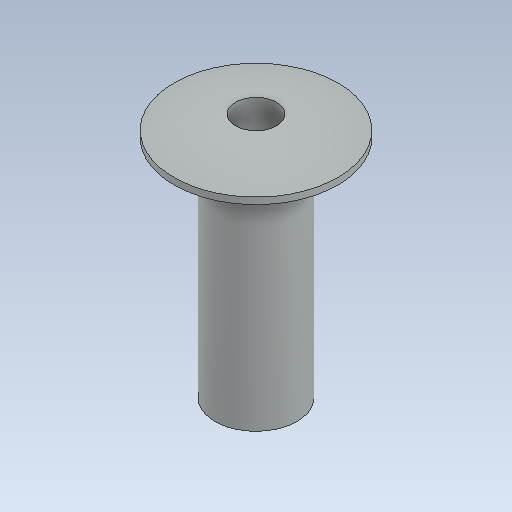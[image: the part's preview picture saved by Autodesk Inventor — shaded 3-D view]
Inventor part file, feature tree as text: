
AUTODESK INVENTOR PART (.ipt)
format: ipt  version: 2023 (Build 270158000, 158)  size: 111,104 bytes
history: native  units: in
note: dims shown in document units (in); Inventor stores cm internally (conversion verified against a paired STEP export)
features: other x1, revolve x1
ambient origin geometry x8: Origin, YZ Plane, XZ Plane, XY Plane, X Axis, Y Axis, Z Axis, Center Point
bodies: Solid1 (feature_tree)
feature tree (2):
  other  "125 rivet.ipt1"
  revolve  "Revolve1"  [1 undecoded]
note: 1 required parameter value undecoded (feature->parameter linkage not recoverable at this tier; creation-order binding heuristic only, values carry confidence <= 0.55)
